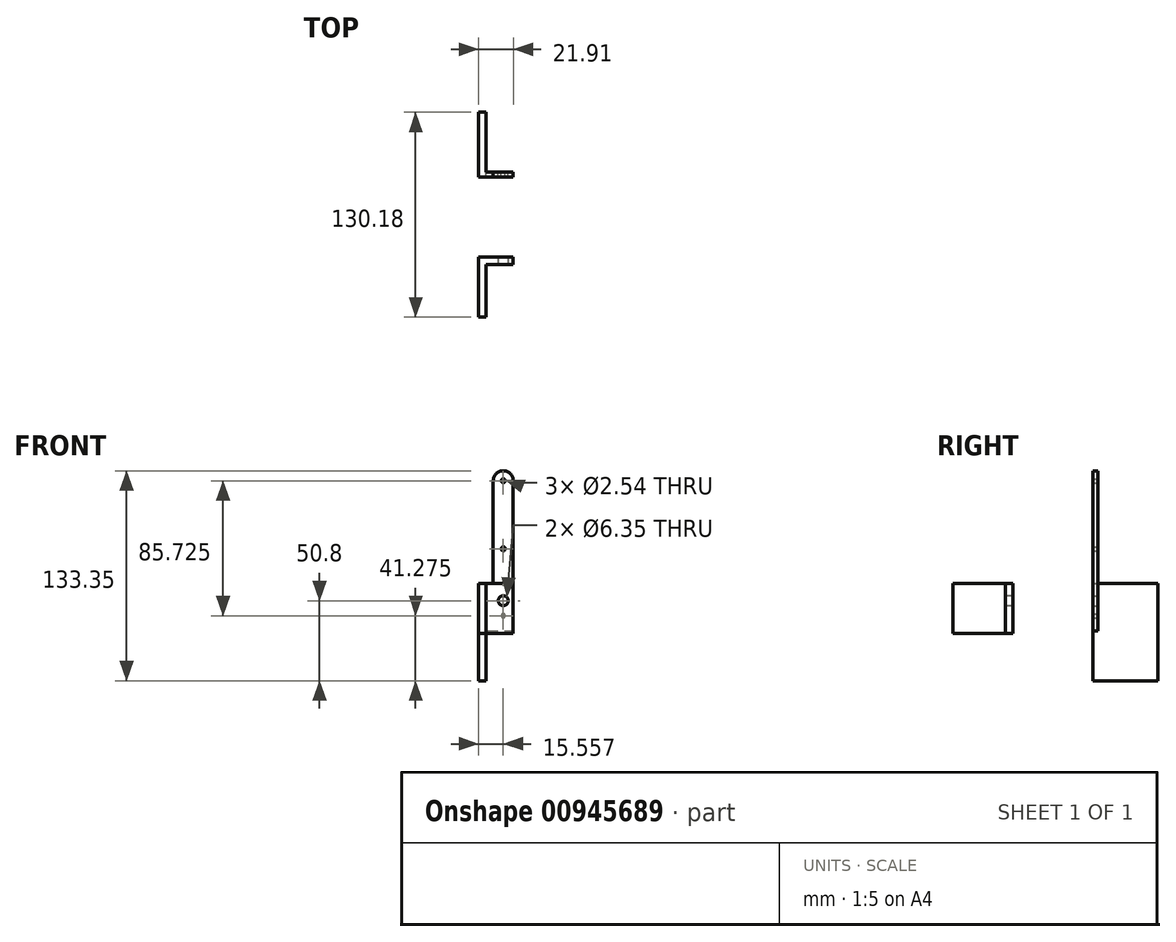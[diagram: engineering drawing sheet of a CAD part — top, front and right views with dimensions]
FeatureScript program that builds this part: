
annotation { "Feature Type Name" : "Feature", "Feature Type Description" : "" }
export const myFeature = defineFeature(function(context is Context, id is Id, definition is map)
    precondition{}
    {
        {
            var Q0;
            Q0=qCreatedBy(makeId("Front.planeOp"),FACE);
            var sketch = newSketch(context, id + "F0", { "sketchPlane" : qUnion([Q0])});
            skLineSegment(sketch, "E0", {"start": v(0, 0) * mm, "end": v(4.76, 0) * mm});
            skLineSegment(sketch, "E1", {"start": v(4.76, 0) * mm, "end": v(4.76, 31.75) * mm});
            skLineSegment(sketch, "E2", {"start": v(4.76, 31.75) * mm, "end": v(21.9, 31.75) * mm});
            skLineSegment(sketch, "E3", {"start": v(21.9, 31.75) * mm, "end": v(21.9, 127) * mm});
            skLineSegment(sketch, "E4", {"start": v(0, 0) * mm, "end": v(0, 61.91) * mm});
            skLineSegment(sketch, "E5", {"start": v(0, 61.91) * mm, "end": v(9.2, 61.91) * mm});
            skLineSegment(sketch, "E6", {"start": v(9.2, 61.91) * mm, "end": v(9.2, 127) * mm});
            skArc(sketch, "E7", {"start": v(21.9, 127) * mm, "mid": v(15.56, 133.35) * mm, "end": v(9.2, 127) * mm});
            skLineSegment(sketch, "E8", {"start": v(4.76, 31.75) * mm, "end": v(4.76, 61.91) * mm});
            skCircle(sketch, "E9", {"center": v(15.56, 127) * mm, "radius": 1.27 * mm});
            skCircle(sketch, "E10", {"center": v(15.56, 83.76) * mm, "radius": 1.27 * mm});
            skCircle(sketch, "E11", {"center": v(15.56, 50.8) * mm, "radius": 3.18 * mm});
            skPoint(sketch, "E12", {"position": v(15.56, 133.35) * mm});
            skCircle(sketch, "E13", {"center": v(15.56, 41.28) * mm, "radius": 1.27 * mm});
            skLineSegment(sketch, "E14", {"start": v(15.56, 50.8) * mm, "end": v(15.56, 41.28) * mm, "construction": true});
            skSolve(sketch);
        }
        {
            var Q0;
            Q0=makeQuery(id+"F0.imprint","IMPRINT",FACE,{"disambiguationData":[TD([[makeQuery(id+"F0.imprint","IMPRINT",EDGE,{"derivedFrom":sQuery(id+"F0.wireOp",EDGE,"E0")}),1.0]])]});
            extrude(context, id + "F1", {"entities" : qUnion([Q0]), "oppositeDirection" : true, "depth" : 38.1 * mm, "offsetDistance" : 25.4 * mm});
        }
        {
            var Q0;
            Q0 = qSketchRegion(id + "F0", true);
            extrude(context, id + "F2", {"entities" : qUnion([Q0]), "operationType" : NewBodyOperationType.ADD, "depth" : 3.17 * mm, "offsetDistance" : 25.4 * mm});
        }
        {
            var Q0;
            Q0=qCreatedBy(makeId("Right.planeOp"),FACE);
            var sketch = newSketch(context, id + "F3", { "sketchPlane" : qUnion([Q0])});
            skPoint(sketch, "E15", {"position": v(-3.18, 61.91) * mm});
            skPoint(sketch, "E16", {"position": v(-3.18, 0) * mm});
            skLineSegment(sketch, "E17", {"start": v(-3.18, 61.91) * mm, "end": v(-53.98, 61.91) * mm, "construction": true});
            skLineSegment(sketch, "E18.bottom", {"start": v(-53.98, 61.91) * mm, "end": v(-92.08, 61.91) * mm});
            skLineSegment(sketch, "E18.left", {"start": v(-53.98, 61.91) * mm, "end": v(-53.98, 30.16) * mm});
            skLineSegment(sketch, "E19", {"start": v(-58.74, 61.91) * mm, "end": v(-58.74, 30.16) * mm});
            skLineSegment(sketch, "E20", {"start": v(-53.98, 30.16) * mm, "end": v(-58.74, 30.16) * mm});
            skLineSegment(sketch, "E21", {"start": v(-92.08, 61.91) * mm, "end": v(-92.08, 30.16) * mm});
            skLineSegment(sketch, "E22", {"start": v(-92.08, 30.16) * mm, "end": v(-58.74, 30.16) * mm});
            skSolve(sketch);
        }
        {
            var Q0;
            {var subQ0=sQuery(id+"F3.wireOp",EDGE,"E18.left");Q0=makeQuery(id+"F3.imprint","IMPRINT",FACE,{"disambiguationData":[TD([[makeQuery(id+"F3.imprint","IMPRINT",EDGE,{"derivedFrom":subQ0}),-1.0]])]});}
            extrude(context, id + "F4", {"entities" : qUnion([Q0]), "depth" : 21.9 * mm, "offsetDistance" : 25.4 * mm});
        }
        {
            var Q0;
            {var subQ2=sQuery(id+"F3.wireOp",EDGE,"E19");Q0=makeQuery(id+"F3.imprint","IMPRINT",FACE,{"disambiguationData":[TD([[makeQuery(id+"F3.imprint","IMPRINT",EDGE,{"derivedFrom":subQ2}),-1.0]])]});}
            extrude(context, id + "F5", {"entities" : qUnion([Q0]), "operationType" : NewBodyOperationType.ADD, "depth" : 4.76 * mm, "offsetDistance" : 25.4 * mm});
        }
        {
            var Q0;
            Q0=makeQuery(id+"F4.opExtrude","SWEPT_FACE",FACE,{"disambiguationData":[OSD([sQuery(id+"F3.wireOp",EDGE,"E19")])]});
            var sketch = newSketch(context, id + "F6", { "sketchPlane" : qUnion([Q0])});
            skPoint(sketch, "E23.0", {"position": v(15.56, 50.8) * mm});
            skCircle(sketch, "E24", {"center": v(15.56, 50.8) * mm, "radius": 3.18 * mm});
            skSolve(sketch);
        }
        {
            var Q0;
            Q0=makeQuery(id+"F6.imprint","IMPRINT",FACE,{"disambiguationData":[TD([[makeQuery(id+"F6.imprint","IMPRINT",EDGE,{"derivedFrom":sQuery(id+"F6.wireOp",EDGE,"E24")}),1.0]])]});
            extrude(context, id + "F7", {"entities" : qUnion([Q0]), "operationType" : NewBodyOperationType.REMOVE, "oppositeDirection" : true, "depth" : 25.4 * mm, "offsetDistance" : 25.4 * mm});
        }
    });
